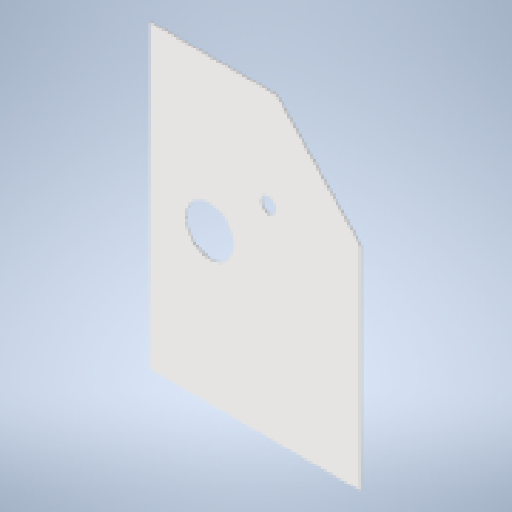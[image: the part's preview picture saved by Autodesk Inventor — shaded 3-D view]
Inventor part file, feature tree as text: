
AUTODESK INVENTOR PART (.ipt)
format: ipt  version: 2024.2 (Build 282272000, 272)  size: 232,960 bytes
history: native  units: mm
features: extrude x3, sketch x2, projected_geometry x1, other x1
ambient origin geometry x8: Origin, YZ Plane, XZ Plane, XY Plane, X Axis, Y Axis, Z Axis, Center Point
bodies: Solid1 (feature_tree)
feature tree (7):
  extrude  "Extrusion1"  Depth=1150.0mm
  extrude  "Extrusion3"  Depth=1180.0mm
  extrude  "Extrusion4"  Depth=950.0mm
  sketch  "Sketch3"  dims[d1=840.0mm d3=1150.0mm]
  sketch  "Sketch4"  dims[d11=390.0mm d12=1180.0mm d13=950.0mm d14=76.0mm d15=1910.0mm d16=255.0mm d17=220.0mm d18=400.0mm d19=220.0mm d21=1277.0mm d22=1554.635823mm d23=100.0mm d24=10.0mm d25=0.0mm d33=2140.0mm d34=494.0mm d37=10.0mm d38=0.0mm d45=310.0mm d47=5.0mm d48=80.0mm d49=372.0mm d51=780.0mm d52=1078.0mm d53=1340.0mm d54=0.0mm d55=0.0mm]
  projected_geometry  "Projected Loop1"
  other  "Definition1"
